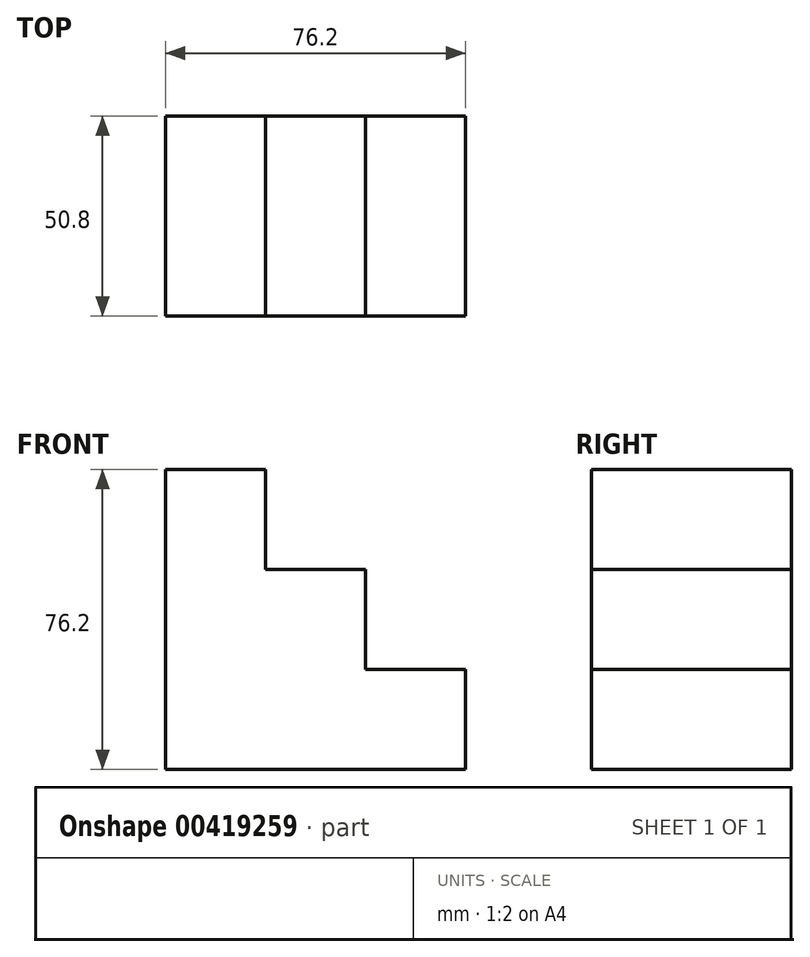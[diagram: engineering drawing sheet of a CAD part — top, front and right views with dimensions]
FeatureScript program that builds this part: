
annotation { "Feature Type Name" : "Feature", "Feature Type Description" : "" }
export const myFeature = defineFeature(function(context is Context, id is Id, definition is map)
    precondition{}
    {
        {
            var Q0;
            Q0=qCreatedBy(makeId("Front.planeOp"),FACE);
            var sketch = newSketch(context, id + "F0", { "sketchPlane" : qUnion([Q0])});
            skLineSegment(sketch, "E0", {"start": v(0, 0) * mm, "end": v(-76.2, 0) * mm});
            skLineSegment(sketch, "E1", {"start": v(-76.2, 0) * mm, "end": v(-76.2, 76.2) * mm});
            skLineSegment(sketch, "E2", {"start": v(0, 0) * mm, "end": v(0, 25.4) * mm});
            skLineSegment(sketch, "E3", {"start": v(0, 25.4) * mm, "end": v(-25.4, 25.4) * mm});
            skLineSegment(sketch, "E4", {"start": v(-25.4, 50.8) * mm, "end": v(-25.4, 25.4) * mm});
            skLineSegment(sketch, "E5", {"start": v(-25.4, 50.8) * mm, "end": v(-50.8, 50.8) * mm});
            skLineSegment(sketch, "E6", {"start": v(-50.8, 50.8) * mm, "end": v(-50.8, 76.2) * mm});
            skLineSegment(sketch, "E7", {"start": v(-76.2, 76.2) * mm, "end": v(-50.8, 76.2) * mm});
            skSolve(sketch);
        }
        {
            var Q0;
            Q0 = qSketchRegion(id + "F0", true);
            extrude(context, id + "F1", {"entities" : qUnion([Q0]), "depth" : 50.8 * mm});
        }
    });
